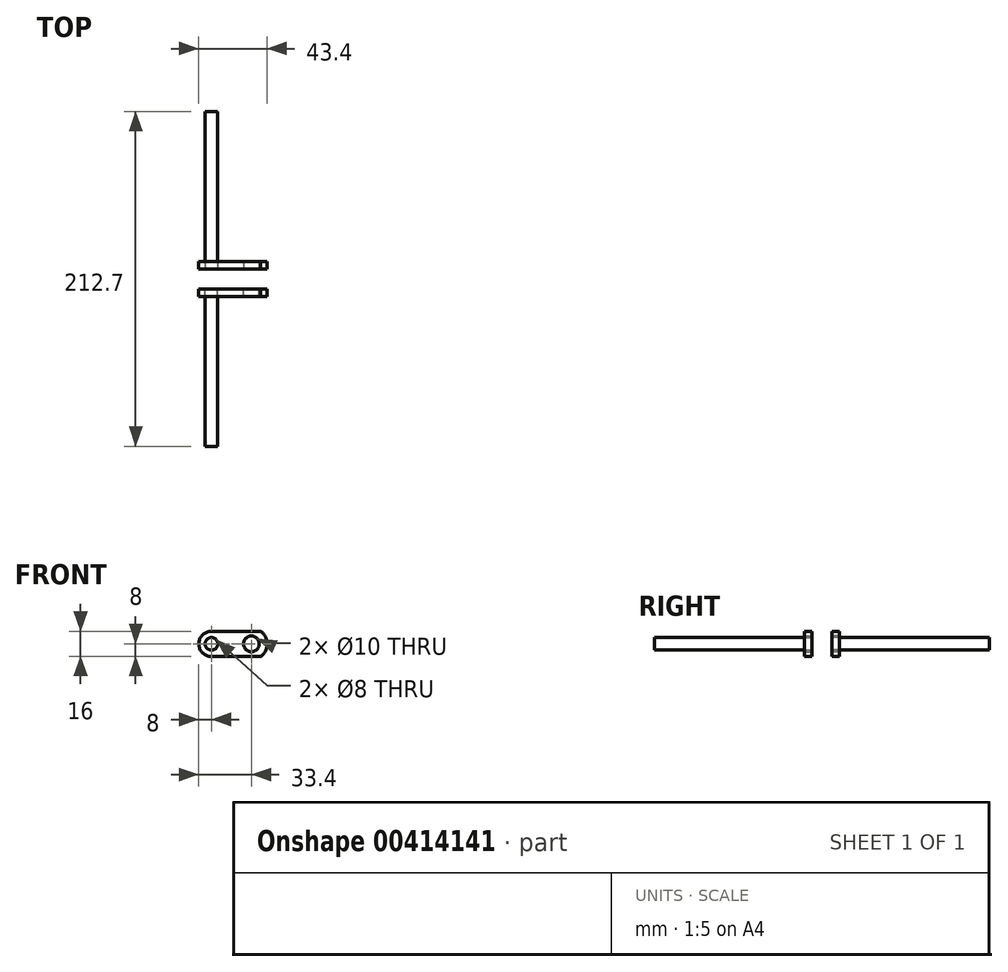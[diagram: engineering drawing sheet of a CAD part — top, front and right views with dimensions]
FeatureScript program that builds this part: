
annotation { "Feature Type Name" : "Feature", "Feature Type Description" : "" }
export const myFeature = defineFeature(function(context is Context, id is Id, definition is map)
    precondition{}
    {
        {
            var Q0;
            Q0=qCreatedBy(makeId("Front.planeOp"),FACE);
            var sketch = newSketch(context, id + "F0", { "sketchPlane" : qUnion([Q0])});
            skCircle(sketch, "E0", {"center": v(0, 0) * mm, "radius": 5 * mm});
            skCircle(sketch, "E1", {"center": v(-25.4, 0) * mm, "radius": 4 * mm});
            skLineSegment(sketch, "E2.bottom", {"start": v(-25.4, 8) * mm, "end": v(6, 8) * mm});
            skLineSegment(sketch, "E2.top", {"start": v(-25.4, -8) * mm, "end": v(6, -8) * mm});
            skLineSegment(sketch, "E3", {"start": v(-25.4, 0) * mm, "end": v(0, 0) * mm, "construction": true});
            skArc(sketch, "E4", {"start": v(-25.4, 8) * mm, "mid": v(-33.4, 0) * mm, "end": v(-25.4, -8) * mm});
            skArc(sketch, "E5", {"start": v(6, 8) * mm, "mid": v(10, 0) * mm, "end": v(6, -8) * mm});
            skSolve(sketch);
        }
        {
            var Q0;
            Q0=qSketchRegion(id+"F0",true);
            extrude(context, id + "F1", {"entities" : qUnion([Q0]), "depth" : 4.76 * mm});
        }
        {
            var Q0;
            Q0=qCreatedBy(makeId("Front.planeOp"),FACE);
            var sketch = newSketch(context, id + "F2", { "sketchPlane" : qUnion([Q0])});
            skCircle(sketch, "E6.0", {"center": v(-25.4, 0) * mm, "radius": 4 * mm});
            skSolve(sketch);
        }
        {
            var Q0;
            Q0=qSketchRegion(id+"F2",true);
            extrude(context, id + "F3", {"entities" : qUnion([Q0]), "depth" : 100 * mm});
        }
        {
            var Q0;
            Q0=qCreatedBy(makeId("Front.planeOp"),FACE);
            cPlane(context, id + "F4", {"entities" : qUnion([Q0]), "cplaneType" : CPlaneType.OFFSET, "offset" : 6.35 * mm, "oppositeDirection" : true, "width" : 150 * mm, "height" : 150 * mm});
        }
        {
            var Q0;
            Q0=makeQuery(id+"F1.opExtrude","SWEPT_BODY",BODY,{"disambiguationData":[OSD([sQuery(id+"F0.wireOp",EDGE,"E0"),sQuery(id+"F0.wireOp",EDGE,"E1"),sQuery(id+"F0.wireOp",EDGE,"E2.bottom"),sQuery(id+"F0.wireOp",EDGE,"E2.top"),sQuery(id+"F0.wireOp",EDGE,"E4"),sQuery(id+"F0.wireOp",EDGE,"E5")])]});
            var Q1;
            Q1=makeQuery(id+"F3.opExtrude","SWEPT_BODY",BODY,{"disambiguationData":[OSD([sQuery(id+"F2.wireOp",EDGE,"E6.0")])]});
            var Q2;
            Q2=qCreatedBy(id+"F4.planeOp",FACE);
            mirror(context, id + "F5", {"entities" : qUnion([Q0, Q1]), "mirrorPlane" : qUnion([Q2])});
        }
    });
